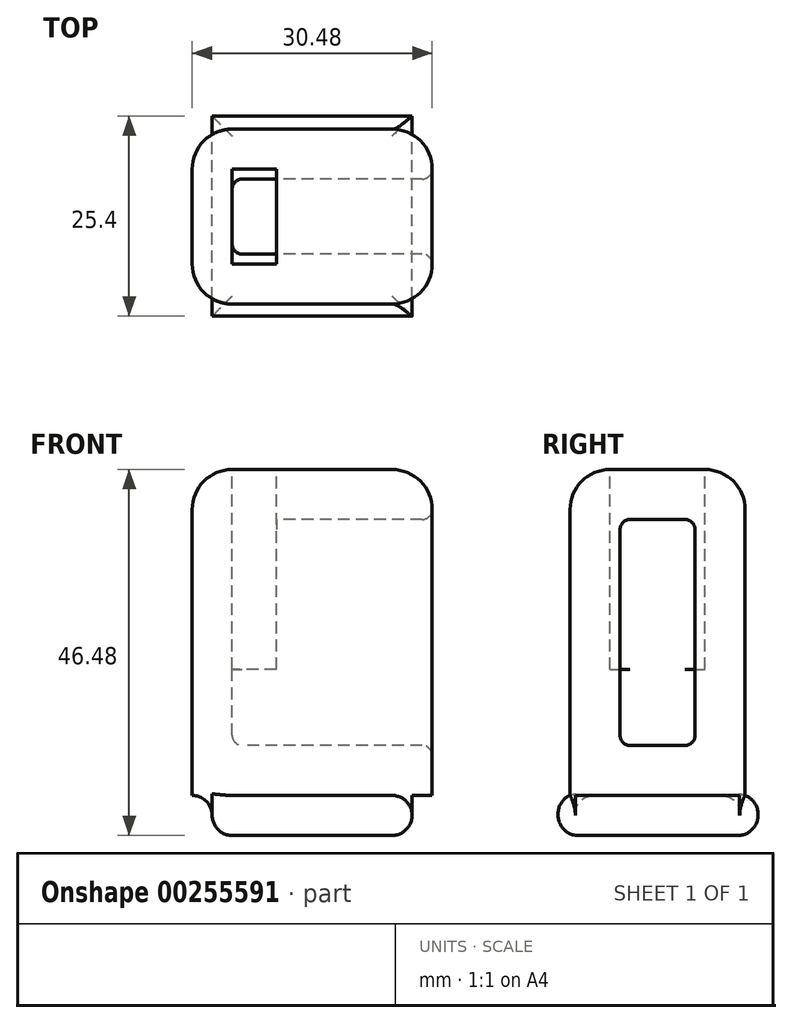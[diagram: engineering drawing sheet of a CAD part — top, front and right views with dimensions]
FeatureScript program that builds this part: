
annotation { "Feature Type Name" : "Feature", "Feature Type Description" : "" }
export const myFeature = defineFeature(function(context is Context, id is Id, definition is map)
    precondition{}
    {
        {
            var Q0;
            Q0=qCreatedBy(makeId("Right.planeOp"),FACE);
            var sketch = newSketch(context, id + "F0", { "sketchPlane" : qUnion([Q0])});
            skLineSegment(sketch, "E0.bottom", {"start": v(0, 0) * mm, "end": v(9.53, 0) * mm});
            skLineSegment(sketch, "E0.top", {"start": v(0, 28.7) * mm, "end": v(9.53, 28.7) * mm});
            skLineSegment(sketch, "E0.left", {"start": v(0, 0) * mm, "end": v(0, 28.7) * mm});
            skLineSegment(sketch, "E0.right", {"start": v(9.53, 0) * mm, "end": v(9.53, 28.7) * mm});
            skLineSegment(sketch, "E1.bottom", {"start": v(-6.35, 35.05) * mm, "end": v(15.88, 35.05) * mm});
            skLineSegment(sketch, "E1.top", {"start": v(-6.35, -6.35) * mm, "end": v(15.88, -6.35) * mm});
            skLineSegment(sketch, "E1.left", {"start": v(-6.35, 35.05) * mm, "end": v(-6.35, -6.35) * mm});
            skLineSegment(sketch, "E1.right", {"start": v(15.88, 35.05) * mm, "end": v(15.88, -6.35) * mm});
            skSolve(sketch);
        }
        {
            var Q0;
            Q0 = qSketchRegion(id + "F0", true);
            extrude(context, id + "F1", {"entities" : qUnion([Q0]), "depth" : 25.4 * mm});
        }
        {
            var Q0;
            Q0=makeQuery(id+"F1.opExtrude","CAP_FACE",FACE,{"disambiguationData":[OSD([sQuery(id+"F0.wireOp",EDGE,"E0.bottom"),sQuery(id+"F0.wireOp",EDGE,"E0.top"),sQuery(id+"F0.wireOp",EDGE,"E0.left"),sQuery(id+"F0.wireOp",EDGE,"E0.right"),sQuery(id+"F0.wireOp",EDGE,"E1.bottom"),sQuery(id+"F0.wireOp",EDGE,"E1.top"),sQuery(id+"F0.wireOp",EDGE,"E1.left"),sQuery(id+"F0.wireOp",EDGE,"E1.right")])],"isStart":true});
            var sketch = newSketch(context, id + "F2", { "sketchPlane" : qUnion([Q0])});
            skLineSegment(sketch, "E2.bottom", {"start": v(-15.88, 35.05) * mm, "end": v(6.35, 35.05) * mm});
            skLineSegment(sketch, "E2.top", {"start": v(-15.87, -6.35) * mm, "end": v(6.35, -6.35) * mm});
            skLineSegment(sketch, "E2.left", {"start": v(-15.88, 35.05) * mm, "end": v(-15.87, -6.35) * mm});
            skLineSegment(sketch, "E2.right", {"start": v(6.35, 35.05) * mm, "end": v(6.35, -6.35) * mm});
            skSolve(sketch);
        }
        {
            var Q0;
            Q0 = qSketchRegion(id + "F2", true);
            extrude(context, id + "F3", {"entities" : qUnion([Q0]), "operationType" : NewBodyOperationType.ADD, "depth" : 5.08 * mm});
        }
        {
            var Q0;
            Q0=makeQuery(id+"F1.opExtrude","SWEPT_FACE",FACE,{"disambiguationData":[OSD([sQuery(id+"F0.wireOp",EDGE,"E0.left")])]});
            var Q1;
            Q1=makeQuery(id+"F3.opExtrude","CAP_FACE",FACE,{"disambiguationData":[OSD([sQuery(id+"F2.wireOp",EDGE,"E2.bottom"),sQuery(id+"F2.wireOp",EDGE,"E2.top"),sQuery(id+"F2.wireOp",EDGE,"E2.left"),sQuery(id+"F2.wireOp",EDGE,"E2.right")])],"isStart":true});
            var Q2;
            Q2=makeQuery(id+"F1.opExtrude","SWEPT_FACE",FACE,{"disambiguationData":[OSD([sQuery(id+"F0.wireOp",EDGE,"E0.right")])]});
            var Q3;
            Q3=makeQuery(id+"F1.opExtrude","SWEPT_FACE",FACE,{"disambiguationData":[OSD([sQuery(id+"F0.wireOp",EDGE,"E0.top")])]});
            var Q4;
            Q4=makeQuery(id+"F1.opExtrude","SWEPT_FACE",FACE,{"disambiguationData":[OSD([sQuery(id+"F0.wireOp",EDGE,"E0.bottom")])]});
            fillet(context, id + "F4", {"entities" : qUnion([Q0, Q1, Q2, Q3, Q4]), "radius" : 1.27 * mm, "tangentPropagation" : true, "allowEdgeOverflow" : false});
        }
        {
            var Q0;
            Q0=makeQuery(id+"F3.boolean.opBoolean","MERGE",FACE,{"derivedFrom":[makeQuery(id+"F1.opExtrude","SWEPT_FACE",FACE,{"disambiguationData":[OSD([sQuery(id+"F0.wireOp",EDGE,"E1.top")])]}),makeQuery(id+"F3.opExtrude","SWEPT_FACE",FACE,{"disambiguationData":[OSD([sQuery(id+"F2.wireOp",EDGE,"E2.top")])]})]});
            var sketch = newSketch(context, id + "F5", { "sketchPlane" : qUnion([Q0])});
            skLineSegment(sketch, "E3.bottom", {"start": v(22.86, 7.87) * mm, "end": v(-2.54, 7.87) * mm});
            skLineSegment(sketch, "E3.top", {"start": v(22.86, -17.53) * mm, "end": v(-2.54, -17.53) * mm});
            skLineSegment(sketch, "E3.left", {"start": v(22.86, 7.87) * mm, "end": v(22.86, -17.53) * mm});
            skLineSegment(sketch, "E3.right", {"start": v(-2.54, 7.87) * mm, "end": v(-2.54, -17.53) * mm});
            skSolve(sketch);
        }
        {
            var Q0;
            Q0 = qSketchRegion(id + "F5", true);
            extrude(context, id + "F6", {"entities" : qUnion([Q0]), "operationType" : NewBodyOperationType.ADD, "depth" : 5.08 * mm});
        }
        {
            var Q0;
            Q0=makeQuery(id+"F6.opExtrude","CAP_FACE",FACE,{"disambiguationData":[OSD([sQuery(id+"F5.wireOp",EDGE,"E3.bottom"),sQuery(id+"F5.wireOp",EDGE,"E3.top"),sQuery(id+"F5.wireOp",EDGE,"E3.left"),sQuery(id+"F5.wireOp",EDGE,"E3.right")])],"isStart":false});
            var Q1;
            Q1=makeQuery(id+"F6.opExtrude","CAP_EDGE",EDGE,{"disambiguationData":[OSD([sQuery(id+"F5.wireOp",EDGE,"E3.top")])],"isStart":true});
            var Q2;
            {var subQ0=sQuery(id+"F5.wireOp",EDGE,"E3.left");Q2=makeQuery(id+"F6.boolean.opBoolean","SPLIT",EDGE,{"disambiguationData":[topologyDisambiguationEdgeConnected([makeQuery(id+"F1.opExtrude","SWEPT_FACE",FACE,{"disambiguationData":[OSD([sQuery(id+"F0.wireOp",EDGE,"E1.top")])]}),makeQuery(id+"F3.opExtrude","SWEPT_FACE",FACE,{"disambiguationData":[OSD([sQuery(id+"F2.wireOp",EDGE,"E2.top")])]}),makeQuery(id+"F6.opExtrude","SWEPT_FACE",FACE,{"disambiguationData":[OSD([subQ0])]})])],"derivedFrom":makeQuery(id+"F6.opExtrude","CAP_EDGE",EDGE,{"disambiguationData":[OSD([subQ0])],"isStart":true})});}
            var Q3;
            Q3=makeQuery(id+"F6.opExtrude","CAP_EDGE",EDGE,{"disambiguationData":[OSD([sQuery(id+"F5.wireOp",EDGE,"E3.bottom")])],"isStart":true});
            var Q4;
            {var subQ0=sQuery(id+"F5.wireOp",EDGE,"E3.right");Q4=makeQuery(id+"F6.boolean.opBoolean","SPLIT",EDGE,{"disambiguationData":[topologyDisambiguationEdgeConnected([makeQuery(id+"F1.opExtrude","SWEPT_FACE",FACE,{"disambiguationData":[OSD([sQuery(id+"F0.wireOp",EDGE,"E1.top")])]}),makeQuery(id+"F3.opExtrude","SWEPT_FACE",FACE,{"disambiguationData":[OSD([sQuery(id+"F2.wireOp",EDGE,"E2.top")])]}),makeQuery(id+"F6.opExtrude","SWEPT_FACE",FACE,{"disambiguationData":[OSD([subQ0])]})])],"derivedFrom":makeQuery(id+"F6.opExtrude","CAP_EDGE",EDGE,{"disambiguationData":[OSD([subQ0])],"isStart":true})});}
            fillet(context, id + "F7", {"entities" : qUnion([Q0, Q1, Q2, Q3, Q4]), "radius" : 2.54 * mm, "tangentPropagation" : true, "allowEdgeOverflow" : false});
        }
        {
            var Q0;
            Q0=makeQuery(id+"F1.opExtrude","CAP_EDGE",EDGE,{"disambiguationData":[OSD([sQuery(id+"F0.wireOp",EDGE,"E1.bottom")])],"isStart":false});
            var Q1;
            Q1=makeQuery(id+"F1.opExtrude","CAP_EDGE",EDGE,{"disambiguationData":[OSD([sQuery(id+"F0.wireOp",EDGE,"E1.left")])],"isStart":false});
            var Q2;
            Q2=makeQuery(id+"F1.opExtrude","CAP_EDGE",EDGE,{"disambiguationData":[OSD([sQuery(id+"F0.wireOp",EDGE,"E1.right")])],"isStart":false});
            fillet(context, id + "F8", {"entities" : qUnion([Q0, Q1, Q2]), "radius" : 5.08 * mm, "tangentPropagation" : true, "allowEdgeOverflow" : false});
        }
        {
            var Q0;
            Q0=makeQuery(id+"F3.boolean.opBoolean","MERGE",EDGE,{"derivedFrom":[makeQuery(id+"F1.opExtrude","SWEPT_EDGE",EDGE,{"disambiguationData":[OSD([sQuery(id+"F0.wireOp",EDGE,"E1.bottom"),sQuery(id+"F0.wireOp",EDGE,"E1.right")])]}),makeQuery(id+"F3.opExtrude","SWEPT_EDGE",EDGE,{"disambiguationData":[OSD([sQuery(id+"F2.wireOp",EDGE,"E2.bottom"),sQuery(id+"F2.wireOp",EDGE,"E2.left")])]})]});
            var Q1;
            Q1=makeQuery(id+"F3.boolean.opBoolean","MERGE",EDGE,{"derivedFrom":[makeQuery(id+"F1.opExtrude","SWEPT_EDGE",EDGE,{"disambiguationData":[OSD([sQuery(id+"F0.wireOp",EDGE,"E1.bottom"),sQuery(id+"F0.wireOp",EDGE,"E1.left")])]}),makeQuery(id+"F3.opExtrude","SWEPT_EDGE",EDGE,{"disambiguationData":[OSD([sQuery(id+"F2.wireOp",EDGE,"E2.bottom"),sQuery(id+"F2.wireOp",EDGE,"E2.right")])]})]});
            var Q2;
            Q2=makeQuery(id+"F3.opExtrude","CAP_EDGE",EDGE,{"disambiguationData":[OSD([sQuery(id+"F2.wireOp",EDGE,"E2.bottom")])],"isStart":false});
            var Q3;
            Q3=makeQuery(id+"F3.opExtrude","CAP_EDGE",EDGE,{"disambiguationData":[OSD([sQuery(id+"F2.wireOp",EDGE,"E2.left")])],"isStart":false});
            var Q4;
            Q4=makeQuery(id+"F3.opExtrude","CAP_EDGE",EDGE,{"disambiguationData":[OSD([sQuery(id+"F2.wireOp",EDGE,"E2.right")])],"isStart":false});
            fillet(context, id + "F9", {"entities" : qUnion([Q0, Q1, Q2, Q3, Q4]), "radius" : 5.08 * mm, "tangentPropagation" : true, "allowEdgeOverflow" : false});
        }
        {
            var Q0;
            Q0=makeQuery(id+"F3.boolean.opBoolean","MERGE",FACE,{"derivedFrom":[makeQuery(id+"F1.opExtrude","SWEPT_FACE",FACE,{"disambiguationData":[OSD([sQuery(id+"F0.wireOp",EDGE,"E1.bottom")])]}),makeQuery(id+"F3.opExtrude","SWEPT_FACE",FACE,{"disambiguationData":[OSD([sQuery(id+"F2.wireOp",EDGE,"E2.bottom")])]})]});
            var sketch = newSketch(context, id + "F10", { "sketchPlane" : qUnion([Q0])});
            skLineSegment(sketch, "E4.bottom", {"start": v(5.62, -1.27) * mm, "end": v(0, -1.27) * mm});
            skLineSegment(sketch, "E4.top", {"start": v(5.62, 10.8) * mm, "end": v(0, 10.8) * mm});
            skLineSegment(sketch, "E4.left", {"start": v(5.62, -1.27) * mm, "end": v(5.62, 10.8) * mm});
            skLineSegment(sketch, "E4.right", {"start": v(0, -1.27) * mm, "end": v(0, 10.8) * mm});
            skSolve(sketch);
        }
        {
            var Q0;
            Q0 = qSketchRegion(id + "F10", true);
            extrude(context, id + "F11", {"entities" : qUnion([Q0]), "operationType" : NewBodyOperationType.REMOVE, "oppositeDirection" : true, "depth" : 25.4 * mm});
        }
    });
